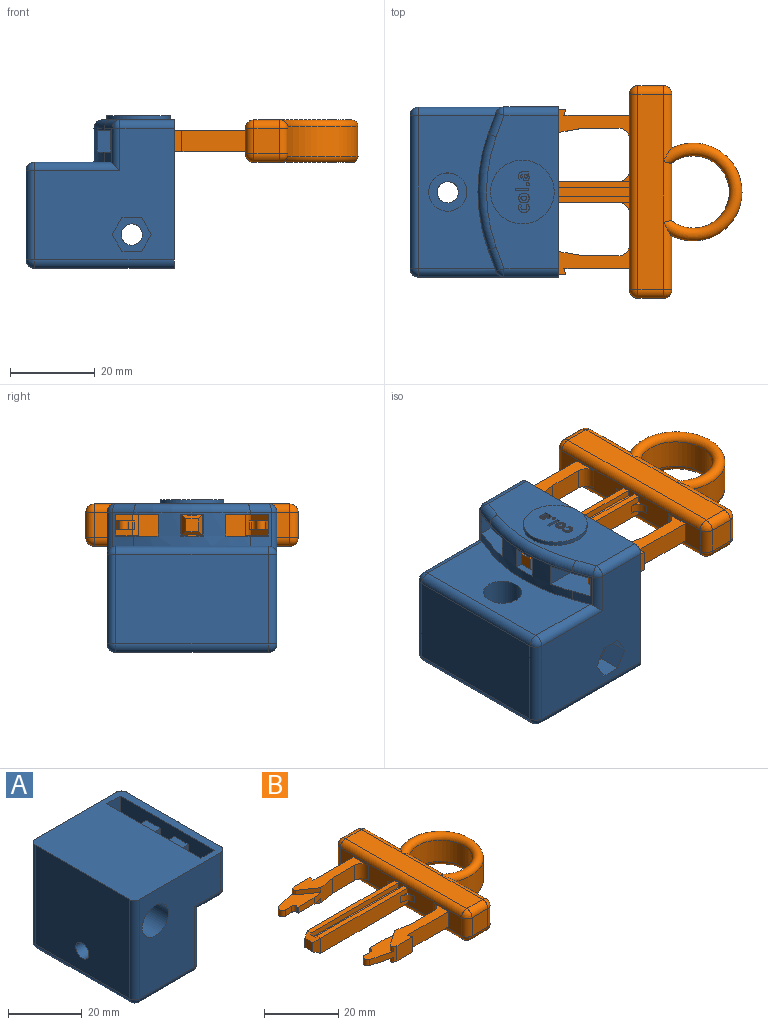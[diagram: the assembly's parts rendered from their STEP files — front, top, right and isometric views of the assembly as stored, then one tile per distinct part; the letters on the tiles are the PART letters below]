
ASSEMBLY  parts=2 mates=1
PART A: 132 faces, bbox 36x40x34.9 mm
  f0: cylinder r=2.5mm len=5mm, axis (0,1,0), area 55mm2, adj f129,f131
  f1: plane 32.88x31mm, normal (0,1,0), area 762.9mm2, adj f5,f23,f27,f32,f34,f35,f123,f124
  f2: plane 2.45x2.1mm, normal (1,0,0), area 3.4mm2, adj f79,f80,f81,f82,f83,f84,f85,f86
  f3: plane 2.44x2.28mm, normal (1,0,0), area 3.4mm2, adj f60,f61,f62,f63,f64,f65,f66,f67
  f4: plane 36x16.88mm, normal (1,0,0), area 379.5mm2, adj f5,f34,f39,f40,f42,f43,f100
  f5: plane 40x35mm, normal (0,0,1), area 1213mm2, adj f1,f4,f8,f10,f14,f15,f16,f19
  f6: plane 8.12x5.01mm, normal (0,0.34,-0.94), area 19.2mm2, adj f7,f14,f15,f16,f20,f32,f35,f40
  f7: cylinder r=40mm len=27.36mm, axis (1,0,0), area 136.1mm2, adj f6,f9,f11,f12,f13,f14,f16,f17
  f8: plane 32.88x31mm, normal (0,-1,0), area 739.7mm2, adj f5,f26,f31,f36,f38,f39,f130
  f9: plane 8.12x5.01mm, normal (0,-0.34,-0.94), area 19.2mm2, adj f7,f10,f14,f16,f20,f36,f38,f43
  f10: plane 14.9x5.1mm, normal (0,1,0), area 76mm2, adj f5,f9,f14,f16
  f11: plane 15.08x5.1mm, normal (0,-1,0), area 76.9mm2, adj f7,f14,f16,f22
  f12: plane 15.8x5.1mm, normal (0,-1,0), area 80.6mm2, adj f7,f14,f16,f21
  f13: plane 15.8x5.1mm, normal (0,1,0), area 80.6mm2, adj f7,f14,f16,f22
  f14: plane 36x18.88mm, normal (-1,0,0), area 464.7mm2, adj f5,f6,f7,f9,f10,f11,f12,f13
  f15: plane 14.9x5.1mm, normal (0,-1,0), area 76mm2, adj f5,f6,f14,f16
  f16: plane 36x18.88mm, normal (1,0,0), area 464.7mm2, adj f5,f6,f7,f9,f10,f11,f12,f13
  f17: plane 15.08x5.1mm, normal (0,1,0), area 76.9mm2, adj f7,f14,f16,f21
  f18: plane 36x21mm, normal (0,0,-1), area 756mm2, adj f25,f27,f30,f31
  f19: plane 36x32.88mm, normal (-1,0,0), area 1164.2mm2, adj f5,f23,f25,f26,f44
  f20: plane 36x17.98mm, normal (1,0,0), area 489.7mm2, adj f6,f7,f9,f30,f32,f36,f46
  f21: plane 5.35x5.1mm, normal (0,0,1), area 27.3mm2, adj f12,f14,f16,f17
  f22: plane 5.35x5.1mm, normal (0,0,1), area 27.3mm2, adj f11,f13,f14,f16
  f23: cylinder r=2mm len=32.88mm, axis (0,0,1), area 103.3mm2, adj f1,f5,f19,f24
  f24: sphere r=2mm, area 6.3mm2, adj f23,f25,f27
  f25: cylinder r=2mm len=36mm, axis (0,1,0), area 113.1mm2, adj f18,f19,f24,f28
  f26: cylinder r=2mm len=32.88mm, axis (0,0,-1), area 103.3mm2, adj f5,f8,f19,f28
  f27: cylinder r=2mm len=21mm, axis (-1,0,0), area 66mm2, adj f1,f18,f24,f29
  f28: sphere r=2mm, area 6.3mm2, adj f25,f26,f31
  f29: sphere r=2mm, area 6.3mm2, adj f27,f30,f32
  f30: cylinder r=2mm len=36mm, axis (0,-1,0), area 113.1mm2, adj f18,f20,f29,f33
  f31: cylinder r=2mm len=21mm, axis (-1,0,0), area 66mm2, adj f8,f18,f28,f33
  f32: cylinder r=2mm len=20.11mm, axis (0,0,-1), area 59.2mm2, adj f1,f6,f20,f29,f35
  f33: sphere r=2mm, area 6.3mm2, adj f30,f31,f36
  f34: cylinder r=2mm len=12.77mm, axis (0,0,1), area 40.1mm2, adj f1,f4,f5,f37
  f35: cylinder r=2mm len=10mm, axis (1,0,0), area 21.8mm2, adj f1,f6,f32,f37
  f36: cylinder r=2mm len=20.11mm, axis (0,0,1), area 59.2mm2, adj f8,f9,f20,f33,f38
  f37: sphere r=2mm, area 4.9mm2, adj f34,f35,f40
  f38: cylinder r=2mm len=10mm, axis (1,0,0), area 21.8mm2, adj f8,f9,f36,f41
  f39: cylinder r=2mm len=12.77mm, axis (0,0,-1), area 40.1mm2, adj f4,f5,f8,f41
  f40: cylinder r=2mm len=5.69mm, axis (0,0.94,0.34), area 16.7mm2, adj f4,f6,f37,f42
  f41: sphere r=2mm, area 4.9mm2, adj f38,f39,f43
  f42: torus R=38mm, axis (1,0,0), area 86.1mm2, adj f4,f7,f40,f43
  f43: cylinder r=2mm len=5.69mm, axis (0,0.94,-0.34), area 16.7mm2, adj f4,f9,f41,f42
  f44: cylinder r=2.5mm len=5mm, axis (1,0,0), area 78.5mm2, adj f19,f45
  f45: plane 9x9mm, normal (1,0,0), area 44mm2, adj f44,f46
  f46: cylinder r=4.5mm len=20mm, axis (1,0,0), area 565.5mm2, adj f20,f45
  f47: extruded ~1x0.4mm, area 0.4mm2, adj f48,f101,f102,f105
  f48: extruded ~1.21x1.1mm, area 1.9mm2, adj f47,f49,f102,f105
  f49: extruded ~1x0.92mm, area 1mm2, adj f48,f50,f102,f105
  f50: extruded ~1x0.86mm, area 0.9mm2, adj f49,f51,f102,f105
  f51: extruded ~1x0.73mm, area 0.8mm2, adj f50,f52,f102,f105
  f52: plane 1x0.5mm, normal (0,0.93,-0.36), area 0.5mm2, adj f51,f53,f102,f105
  f53: extruded ~1x0.28mm, area 0.3mm2, adj f52,f54,f102,f105
  f54: extruded ~1x0.26mm, area 0.3mm2, adj f53,f55,f102,f105
  f55: extruded ~1x0.71mm, area 1mm2, adj f54,f56,f102,f105
  f56: extruded ~1x0.69mm, area 1mm2, adj f55,f57,f102,f105
  f57: extruded ~1x0.34mm, area 0.3mm2, adj f56,f58,f102,f105
  f58: extruded ~1x0.32mm, area 0.4mm2, adj f57,f59,f102,f105
  f59: plane 1x0.55mm, normal (0,1,0), area 0.6mm2, adj f58,f101,f102,f105
  f60: extruded ~1x0.65mm, area 0.7mm2, adj f3,f61,f96,f102
  f61: extruded ~1x0.9mm, area 1mm2, adj f3,f60,f62,f102
  f62: extruded ~1x0.85mm, area 0.9mm2, adj f3,f61,f63,f102
  f63: extruded ~1x0.6mm, area 0.6mm2, adj f3,f62,f64,f102
  f64: extruded ~1x0.43mm, area 0.6mm2, adj f3,f63,f65,f102
  f65: extruded ~1x0.65mm, area 0.7mm2, adj f3,f64,f66,f102
  f66: extruded ~1x0.9mm, area 1mm2, adj f3,f65,f67,f102
  f67: extruded ~1x0.85mm, area 0.9mm2, adj f3,f66,f68,f102
  f68: extruded ~1x0.6mm, area 0.6mm2, adj f3,f67,f96,f102
  f69: plane 3.28x1mm, normal (0,1,0), area 3.3mm2, adj f70,f97,f102,f104
  f70: plane 1x0.64mm, normal (0,0,-1), area 0.6mm2, adj f69,f71,f102,f104
  f71: plane 3.28x1mm, normal (0,-1,0), area 3.3mm2, adj f70,f97,f102,f104
  f72: extruded ~1x0.26mm, area 0.3mm2, adj f73,f98,f102,f103
  f73: extruded ~1x0.27mm, area 0.3mm2, adj f72,f74,f102,f103
  f74: extruded ~1x0.28mm, area 0.3mm2, adj f73,f75,f102,f103
  f75: extruded ~1x0.27mm, area 0.3mm2, adj f74,f76,f102,f103
  f76: extruded ~1x0.27mm, area 0.3mm2, adj f75,f77,f102,f103
  f77: extruded ~1x0.26mm, area 0.3mm2, adj f76,f78,f102,f103
  f78: extruded ~1x0.27mm, area 0.3mm2, adj f77,f98,f102,f103
  f79: plane 1x0.45mm, normal (0,0,-1), area 0.4mm2, adj f2,f80,f99,f102
  f80: plane 1x0.32mm, normal (0,-0.93,-0.36), area 0.3mm2, adj f2,f79,f81,f102
  f81: plane 1x0.02mm, normal (0,0,-1), area 0mm2, adj f2,f80,f82,f102
  f82: extruded ~1x0.33mm, area 0.4mm2, adj f2,f81,f83,f102
  f83: extruded ~1x0.45mm, area 0.5mm2, adj f2,f82,f84,f102
  f84: extruded ~1x0.53mm, area 0.6mm2, adj f2,f83,f85,f102
  f85: extruded ~1x0.55mm, area 0.6mm2, adj f2,f84,f86,f102
  f86: extruded ~1x0.55mm, area 0.6mm2, adj f2,f85,f87,f102
  f87: extruded ~1x0.79mm, area 0.8mm2, adj f2,f86,f88,f102
  f88: plane 1x0.41mm, normal (0,-0.03,1), area 0.4mm2, adj f2,f87,f89,f102
  f89: plane 1x0.1mm, normal (0,-1,0), area 0.1mm2, adj f2,f88,f90,f102
  f90: extruded ~1x0.37mm, area 0.6mm2, adj f2,f89,f91,f102
  f91: extruded ~1x0.66mm, area 0.7mm2, adj f2,f90,f92,f102
  f92: plane 1x0.43mm, normal (0,-0.9,-0.44), area 0.5mm2, adj f2,f91,f93,f102
  f93: extruded ~1x0.9mm, area 0.9mm2, adj f2,f92,f94,f102
  f94: extruded ~1x0.73mm, area 0.8mm2, adj f2,f93,f95,f102
  f95: extruded ~1x0.63mm, area 0.7mm2, adj f2,f94,f99,f102
  f96: extruded ~1x0.42mm, area 0.6mm2, adj f3,f60,f68,f102
  f97: plane 1x0.64mm, normal (0,0,1), area 0.6mm2, adj f69,f71,f102,f104
  f98: extruded ~1x0.27mm, area 0.3mm2, adj f72,f78,f102,f103
  f99: plane 1.57x1mm, normal (0,1,0), area 1.6mm2, adj f2,f79,f95,f102
  f100: cylinder r=7.5mm len=15mm, axis (-1,0,0), area 47.1mm2, adj f4,f102
  f101: extruded ~1x0.32mm, area 0.3mm2, adj f47,f59,f102,f105
  f102: plane 15x15mm, normal (1,0,0), area 163.3mm2, adj f47,f48,f49,f50,f51,f52,f53,f54
  f103: plane 0.74x0.72mm, normal (1,0,0), area 0.4mm2, adj f72,f73,f74,f75,f76,f77,f78,f98
  f104: plane 3.28x0.64mm, normal (1,0,0), area 2.1mm2, adj f69,f70,f71,f97
  f105: plane 2.44x1.89mm, normal (1,0,0), area 2.5mm2, adj f47,f48,f49,f50,f51,f52,f53,f54
  f106: extruded ~1x0.53mm, area 0.5mm2, adj f3,f107,f113,f114
  f107: extruded ~1x0.53mm, area 0.5mm2, adj f3,f106,f108,f114
  f108: extruded ~1x0.37mm, area 0.4mm2, adj f3,f107,f109,f114
  f109: extruded ~1x0.37mm, area 0.4mm2, adj f3,f108,f110,f114
  f110: extruded ~1x0.53mm, area 0.5mm2, adj f3,f109,f111,f114
  f111: extruded ~1x0.53mm, area 0.5mm2, adj f3,f110,f112,f114
  f112: extruded ~1x0.37mm, area 0.4mm2, adj f3,f111,f113,f114
  f113: extruded ~1x0.37mm, area 0.4mm2, adj f3,f106,f112,f114
  f114: plane 1.41x0.97mm, normal (1,0,0), area 1.2mm2, adj f106,f107,f108,f109,f110,f111,f112,f113
  f115: plane 1x0.19mm, normal (0,-1,0), area 0.2mm2, adj f2,f116,f121,f122
  f116: plane 1x0.25mm, normal (0,0.04,-1), area 0.2mm2, adj f2,f115,f117,f122
  f117: extruded ~1x0.42mm, area 0.4mm2, adj f2,f116,f118,f122
  f118: extruded ~1x0.28mm, area 0.3mm2, adj f2,f117,f119,f122
  f119: extruded ~1x0.31mm, area 0.5mm2, adj f2,f118,f120,f122
  f120: extruded ~1x0.36mm, area 0.4mm2, adj f2,f119,f121,f122
  f121: extruded ~1x0.34mm, area 0.4mm2, adj f2,f115,f120,f122
  f122: plane 0.8x0.66mm, normal (1,0,0), area 0.4mm2, adj f115,f116,f117,f118,f119,f120,f121
  f123: plane 5.5x4.62mm, normal (-1,0,0), area 25.4mm2, adj f1,f124,f128,f129
  f124: plane 5.5x4mm, normal (-0.5,0,0.87), area 25.4mm2, adj f1,f123,f125,f129
  f125: plane 5.5x4mm, normal (0.5,0,0.87), area 25.4mm2, adj f1,f124,f126,f129
  f126: plane 5.5x4.62mm, normal (1,0,0), area 25.4mm2, adj f1,f125,f127,f129
  f127: plane 5.5x4mm, normal (0.5,0,-0.87), area 25.4mm2, adj f1,f126,f128,f129
  f128: plane 5.5x4mm, normal (-0.5,0,-0.87), area 25.4mm2, adj f1,f123,f127,f129
  f129: plane 9.24x8mm, normal (0,1,0), area 35.8mm2, adj f0,f123,f124,f125,f126,f127,f128
  f130: cylinder r=5mm len=31mm, axis (0,-1,0), area 973.9mm2, adj f8,f131
  f131: plane 10x10mm, normal (0,-1,0), area 58.9mm2, adj f0,f130
PART B: 101 faces, bbox 62.4x50x10 mm
  f0: plane 13.75x6mm, normal (1,0,0), area 82.5mm2, adj f2,f4,f100
  f1: plane 12.64x6mm, normal (1,0,0), area 75.9mm2, adj f3,f77,f83,f98
  f2: cylinder r=2mm len=14.28mm, axis (0,-1,0), area 43.3mm2, adj f0,f14,f97,f100
  f3: cylinder r=2mm len=15.86mm, axis (0,-1,0), area 42.8mm2, adj f1,f14,f78,f97,f98
  f4: cylinder r=2mm len=14.28mm, axis (0,1,0), area 43.3mm2, adj f0,f15,f99,f100
  f5: cylinder r=2mm len=15.86mm, axis (0,1,0), area 42.8mm2, adj f12,f15,f88,f98,f99
  f6: plane 33x1.5mm, normal (0,0,-1), area 49.5mm2, adj f10,f62,f63,f75
  f7: plane 33x1.5mm, normal (0,0,1), area 49.5mm2, adj f10,f56,f60,f74
  f8: plane 13.64x5.73mm, normal (0,0,1), area 43.4mm2, adj f22,f28,f29,f30,f31,f32,f33,f53
  f9: plane 13.64x5.73mm, normal (0,0,-1), area 43.4mm2, adj f22,f28,f29,f30,f31,f32,f33,f50
  f10: plane 46x6mm, normal (-1,0,0), area 192mm2, adj f6,f7,f16,f17,f18,f19,f20,f21
  f11: plane 6x6mm, normal (0,-1,0), area 36mm2, adj f82,f91,f92,f96
  f12: plane 12.64x6mm, normal (1,0,0), area 75.9mm2, adj f5,f81,f82,f98
  f13: plane 6x6mm, normal (0,1,0), area 36mm2, adj f77,f80,f84,f85
  f14: plane 46x6mm, normal (0,0,1), area 276mm2, adj f2,f3,f80,f81,f90,f91
  f15: plane 46x6mm, normal (0,0,-1), area 276mm2, adj f4,f5,f83,f84,f92,f93
  f16: cylinder r=2.5mm len=2.5mm, axis (0,0,-1), area 7.9mm2, adj f10,f17,f18,f62
  f17: plane 2.5x2.5mm, normal (0,0,1), area 1.3mm2, adj f10,f16,f62
  f18: plane 2.5x2.5mm, normal (0,0,-1), area 1.3mm2, adj f10,f16,f62
  f19: cylinder r=2.5mm len=2.5mm, axis (0,0,-1), area 7.9mm2, adj f10,f20,f21,f60
  f20: plane 2.5x2.5mm, normal (0,0,1), area 1.3mm2, adj f10,f19,f60
  f21: plane 2.5x2.5mm, normal (0,0,-1), area 1.3mm2, adj f10,f19,f60
  f22: plane 8.14x5mm, normal (-0.26,-0.97,0), area 20mm2, adj f8,f9,f23,f33,f50,f52,f54,f55
  f23: plane 6x5mm, normal (0,-1,0), area 30mm2, adj f22,f24,f52,f55
  f24: plane 5x1.5mm, normal (0.97,0.26,0), area 7.8mm2, adj f23,f25,f52,f55
  f25: plane 15.4x5mm, normal (0,-1,0), area 77mm2, adj f10,f24,f52,f55
  f26: cylinder r=2.5mm len=5mm, axis (0,0,-1), area 19.6mm2, adj f10,f27,f52,f55
  f27: plane 8.5x5mm, normal (0,1,0), area 42.5mm2, adj f26,f28,f52,f55
  f28: plane 8.51x5mm, normal (0.17,0.98,0), area 33.6mm2, adj f8,f9,f27,f29,f51,f52,f53,f55
  f29: plane 6x2mm, normal (0,1,0), area 12mm2, adj f8,f9,f28,f30
  f30: plane 2x0.5mm, normal (-1,0,0), area 1mm2, adj f8,f9,f29,f31
  f31: cylinder r=1mm len=2mm, axis (0,0,-1), area 3.1mm2, adj f8,f9,f30,f32
  f32: plane 2.32x2mm, normal (0,1,0), area 4.6mm2, adj f8,f9,f31,f33
  f33: cylinder r=1.18mm len=2.32mm, axis (0,0,-1), area 6.8mm2, adj f8,f9,f22,f32
  f34: plane 33.5x2mm, normal (0,0,1), area 67mm2, adj f10,f56,f57,f58
  f35: plane 33.5x2mm, normal (0,0,-1), area 67mm2, adj f10,f59,f63,f64
  f36: plane 6x5mm, normal (0,1,0), area 30mm2, adj f37,f47,f69,f72
  f37: plane 8.14x5mm, normal (-0.26,0.97,0), area 20mm2, adj f36,f38,f48,f49,f67,f69,f71,f72
  f38: cylinder r=1.18mm len=2.32mm, axis (0,0,-1), area 6.8mm2, adj f37,f39,f48,f49
  f39: plane 2.32x2mm, normal (0,-1,0), area 4.6mm2, adj f38,f40,f48,f49
  f40: cylinder r=1mm len=2mm, axis (0,0,-1), area 3.1mm2, adj f39,f41,f48,f49
  f41: plane 2x0.5mm, normal (-1,0,0), area 1mm2, adj f40,f42,f48,f49
  f42: plane 6x2mm, normal (0,-1,0), area 12mm2, adj f41,f43,f48,f49
  f43: plane 8.51x5mm, normal (0.17,-0.98,0), area 33.6mm2, adj f42,f44,f48,f49,f68,f69,f70,f72
  f44: plane 8.5x5mm, normal (0,-1,0), area 42.5mm2, adj f43,f45,f69,f72
  f45: cylinder r=2.5mm len=5mm, axis (0,0,-1), area 19.6mm2, adj f10,f44,f69,f72
  f46: plane 15.4x5mm, normal (0,1,0), area 77mm2, adj f10,f47,f69,f72
  f47: plane 5x1.5mm, normal (0.97,-0.26,0), area 7.8mm2, adj f36,f46,f69,f72
  f48: plane 13.64x5.73mm, normal (0,0,1), area 43.4mm2, adj f37,f38,f39,f40,f41,f42,f43,f70
  f49: plane 13.64x5.73mm, normal (0,0,-1), area 43.4mm2, adj f37,f38,f39,f40,f41,f42,f43,f67
  f50: cylinder r=0.75mm len=1.5mm, axis (0,0,-1), area 2.2mm2, adj f9,f22,f51,f52
  f51: plane 5.64x3.95mm, normal (-0.57,0.82,0), area 10.3mm2, adj f9,f28,f50,f52
  f52: plane 22.33x7mm, normal (0,0,-1), area 74.5mm2, adj f10,f22,f23,f24,f25,f26,f27,f28
  f53: plane 5.64x3.95mm, normal (-0.57,0.82,0), area 10.3mm2, adj f8,f28,f54,f55
  f54: cylinder r=0.75mm len=1.5mm, axis (0,0,-1), area 2.2mm2, adj f8,f22,f53,f55
  f55: plane 22.33x7mm, normal (0,0,1), area 74.5mm2, adj f10,f22,f23,f24,f25,f26,f27,f28
  f56: plane 33.5x1.5mm, normal (0,-1,0), area 50.2mm2, adj f7,f10,f34,f57,f74
  f57: plane 2x1.25mm, normal (1,0,0), area 2.5mm2, adj f34,f56,f58,f74
  f58: plane 33.5x1.5mm, normal (0,1,0), area 50.2mm2, adj f10,f34,f57,f65,f74
  f59: plane 33.5x1.5mm, normal (0,-1,0), area 50.2mm2, adj f10,f35,f64,f66,f75
  f60: plane 33x5mm, normal (0,1,0), area 160mm2, adj f7,f10,f19,f20,f21,f66,f76
  f61: plane 3x3mm, normal (-1,0,0), area 9mm2, adj f73,f74,f75,f76
  f62: plane 33x5mm, normal (0,-1,0), area 160mm2, adj f6,f10,f16,f17,f18,f65,f73
  f63: plane 33.5x1.5mm, normal (0,1,0), area 50.2mm2, adj f6,f10,f35,f64,f75
  f64: plane 2x1.25mm, normal (1,0,0), area 2.5mm2, adj f35,f59,f63,f75
  f65: plane 33x1.5mm, normal (0,0,1), area 49.5mm2, adj f10,f58,f62,f74
  f66: plane 33x1.5mm, normal (0,0,-1), area 49.5mm2, adj f10,f59,f60,f75
  f67: cylinder r=0.75mm len=1.5mm, axis (0,0,-1), area 2.2mm2, adj f37,f49,f68,f69
  f68: plane 5.64x3.95mm, normal (-0.57,-0.82,0), area 10.3mm2, adj f43,f49,f67,f69
  f69: plane 22.33x7mm, normal (0,0,-1), area 74.5mm2, adj f10,f36,f37,f43,f44,f45,f46,f47
  f70: plane 5.64x3.95mm, normal (-0.57,-0.82,0), area 10.3mm2, adj f43,f48,f71,f72
  f71: cylinder r=0.75mm len=1.5mm, axis (0,0,-1), area 2.2mm2, adj f37,f48,f70,f72
  f72: plane 22.33x7mm, normal (0,0,1), area 74.5mm2, adj f10,f36,f37,f43,f44,f45,f46,f47
  f73: plane 5x2mm, normal (-0.45,-0.89,0), area 8.9mm2, adj f61,f62,f74,f75
  f74: plane 5x2mm, normal (-0.45,0,0.89), area 7.8mm2, adj f7,f56,f57,f58,f61,f65,f73,f76
  f75: plane 5x2mm, normal (-0.45,0,-0.89), area 7.8mm2, adj f6,f59,f61,f63,f64,f66,f73,f76
  f76: plane 5x2mm, normal (-0.45,0.89,0), area 8.9mm2, adj f60,f61,f74,f75
  f77: cylinder r=2mm len=6mm, axis (0,0,-1), area 18.8mm2, adj f1,f13,f78,f79
  f78: sphere r=2mm, area 6.3mm2, adj f3,f77,f80
  f79: sphere r=2mm, area 6.3mm2, adj f77,f83,f84
  f80: cylinder r=2mm len=6mm, axis (1,0,0), area 18.8mm2, adj f13,f14,f78,f86
  f81: cylinder r=2mm len=15.86mm, axis (0,-1,0), area 42.8mm2, adj f12,f14,f87,f97,f98
  f82: cylinder r=2mm len=6mm, axis (0,0,1), area 18.8mm2, adj f11,f12,f87,f88
  f83: cylinder r=2mm len=15.86mm, axis (0,1,0), area 42.8mm2, adj f1,f15,f79,f98,f99
  f84: cylinder r=2mm len=6mm, axis (-1,0,0), area 18.8mm2, adj f13,f15,f79,f89
  f85: cylinder r=2mm len=6mm, axis (0,0,1), area 18.8mm2, adj f10,f13,f86,f89
  f86: sphere r=2mm, area 6.3mm2, adj f80,f85,f90
  f87: sphere r=2mm, area 6.3mm2, adj f81,f82,f91
  f88: sphere r=2mm, area 6.3mm2, adj f5,f82,f92
  f89: sphere r=2mm, area 6.3mm2, adj f84,f85,f93
  f90: cylinder r=2mm len=46mm, axis (0,1,0), area 144.5mm2, adj f10,f14,f86,f94
  f91: cylinder r=2mm len=6mm, axis (-1,0,0), area 18.8mm2, adj f11,f14,f87,f94
  f92: cylinder r=2mm len=6mm, axis (1,0,0), area 18.8mm2, adj f11,f15,f88,f95
  f93: cylinder r=2mm len=46mm, axis (0,-1,0), area 144.5mm2, adj f10,f15,f89,f95
  f94: sphere r=2mm, area 6.3mm2, adj f90,f91,f96
  f95: sphere r=2mm, area 6.3mm2, adj f92,f93,f96
  f96: cylinder r=2mm len=6mm, axis (0,0,-1), area 18.8mm2, adj f10,f11,f94,f95
  f97: torus R=10mm, axis (0,0,-1), area 207.2mm2, adj f2,f3,f81,f98,f100
  f98: cylinder r=11.5mm len=23mm, axis (0,0,-1), area 325.4mm2, adj f1,f3,f5,f12,f81,f83,f97,f99
  f99: torus R=10mm, axis (0,0,-1), area 207.2mm2, adj f4,f5,f83,f98,f100
  f100: cylinder r=8.5mm len=17mm, axis (0,0,-1), area 261.8mm2, adj f0,f2,f4,f97,f99
PLACE A rot(axis=(-0.71,0,-0.71),180deg) t=(196.6,-56.01,198.16)mm fixed
PLACE B t=(218.35,-56.01,143.11)mm
MATE slider B.f61 <-> A.f5  axis (-1,0,0) through (178.35,-56.01,143.11)mm
